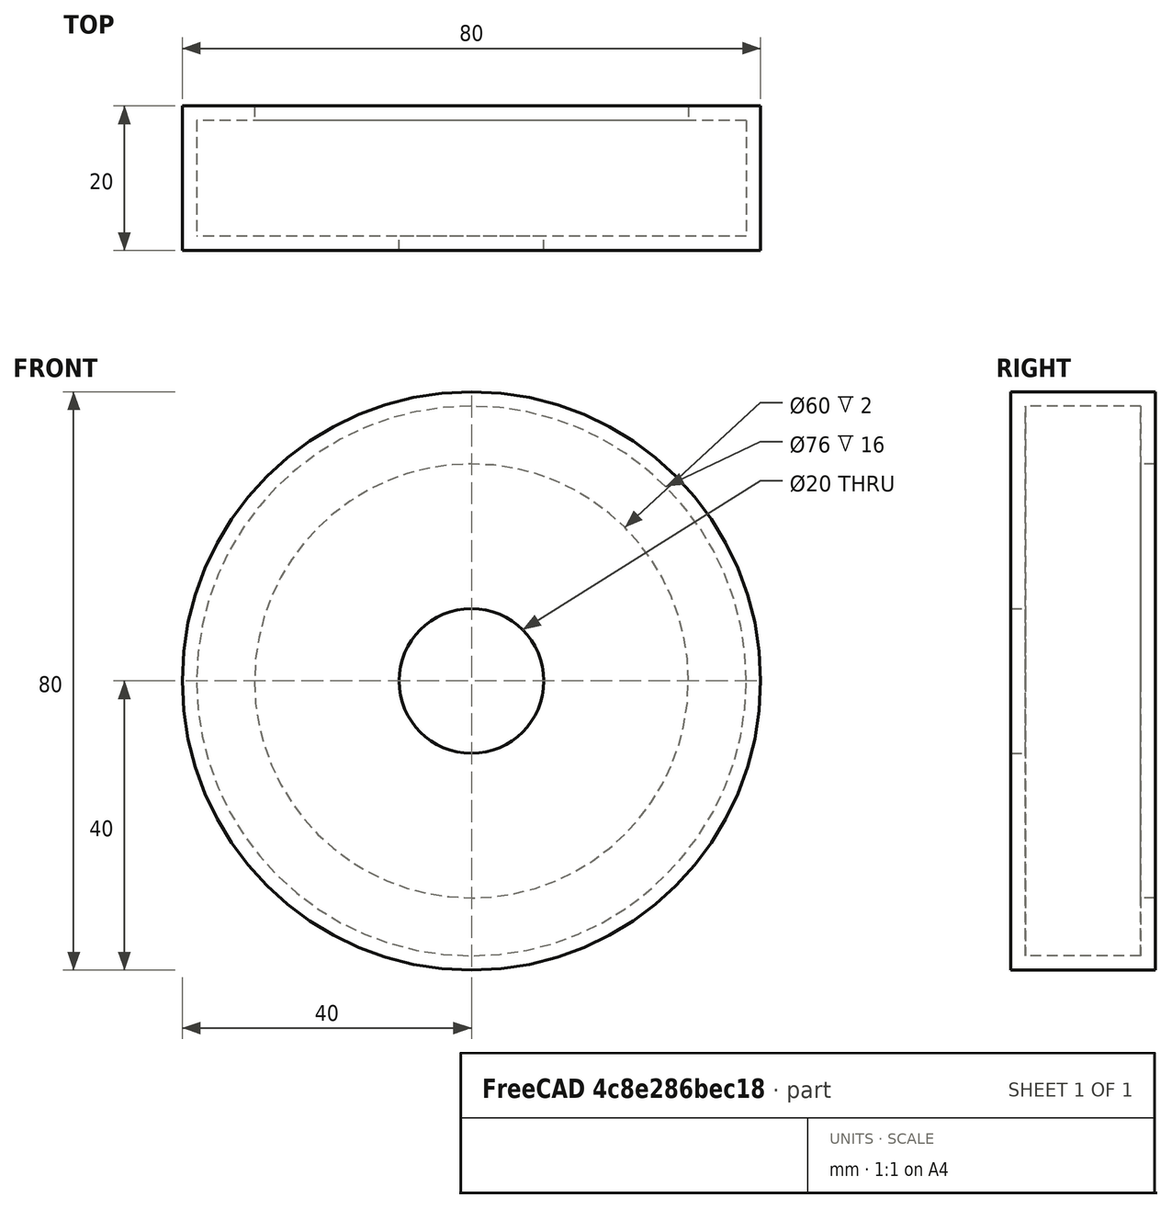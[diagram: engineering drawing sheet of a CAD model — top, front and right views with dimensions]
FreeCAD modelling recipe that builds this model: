
FCSTD DOCUMENT
Label: highbase
objects: Sketcher::SketchObject×1, Part::Revolution×1
note: 2 computed .brp shape members not serialized (recipe doc carries the construction recipe); baked Part::Feature solids carry a one-line shape summary decoded from their .brp

FEATURE [Sketcher::SketchObject] Sketch
  sketch-geometry (8):
    g0: LineSegment StartX=10 StartY=0 StartZ=0 EndX=40 EndY=0 EndZ=0
    g1: LineSegment StartX=40 StartY=0 StartZ=0 EndX=40 EndY=20 EndZ=0
    g2: LineSegment StartX=40 StartY=20 StartZ=0 EndX=30 EndY=20 EndZ=0
    g3: LineSegment StartX=30 StartY=20 StartZ=0 EndX=30 EndY=18 EndZ=0
    g4: LineSegment StartX=30 StartY=18 StartZ=0 EndX=38 EndY=18 EndZ=0
    g5: LineSegment StartX=38 StartY=18 StartZ=0 EndX=38 EndY=2 EndZ=0
    g6: LineSegment StartX=10 StartY=0 StartZ=0 EndX=10 EndY=2 EndZ=0
    g7: LineSegment StartX=38 StartY=2 StartZ=0 EndX=10 EndY=2 EndZ=0
  constraints (24):
    c: Horizontal(g0)
    c: Coincident(g1,g0)
    c: Vertical(g1)
    c: Horizontal(g2)
    c: Coincident(g3,g2)
    c: Horizontal(g4)
    c: Coincident(g5,g4)
    c: Vertical(g5)
    c: Coincident(g6,g0)
    c: Coincident(g7,g5)
    c: Coincident(g7,g6)
    c: Horizontal(g7)
    c: Distance(g0) = 30
    c: Distance(g7) = 28
    c: Parallel(g6,g1)
    c: Coincident(g1,g2)
    c: Parallel(g3,g6)
    c: Distance(g2) = 10
    c: Coincident(g3,g4)
    c: Distance(g3) = 2
    c: Distance(g6) = 2
    c: Distance(g1) = 20
    c: Distance(g-1,g0) = 10
    c: DistanceY(g-1,g0) = 0
FEATURE [Part::Revolution] Revolve
  Angle = 360
  Axis = (0,1,0)
  Base = (0,0,0)
  Source = -> Sketch
